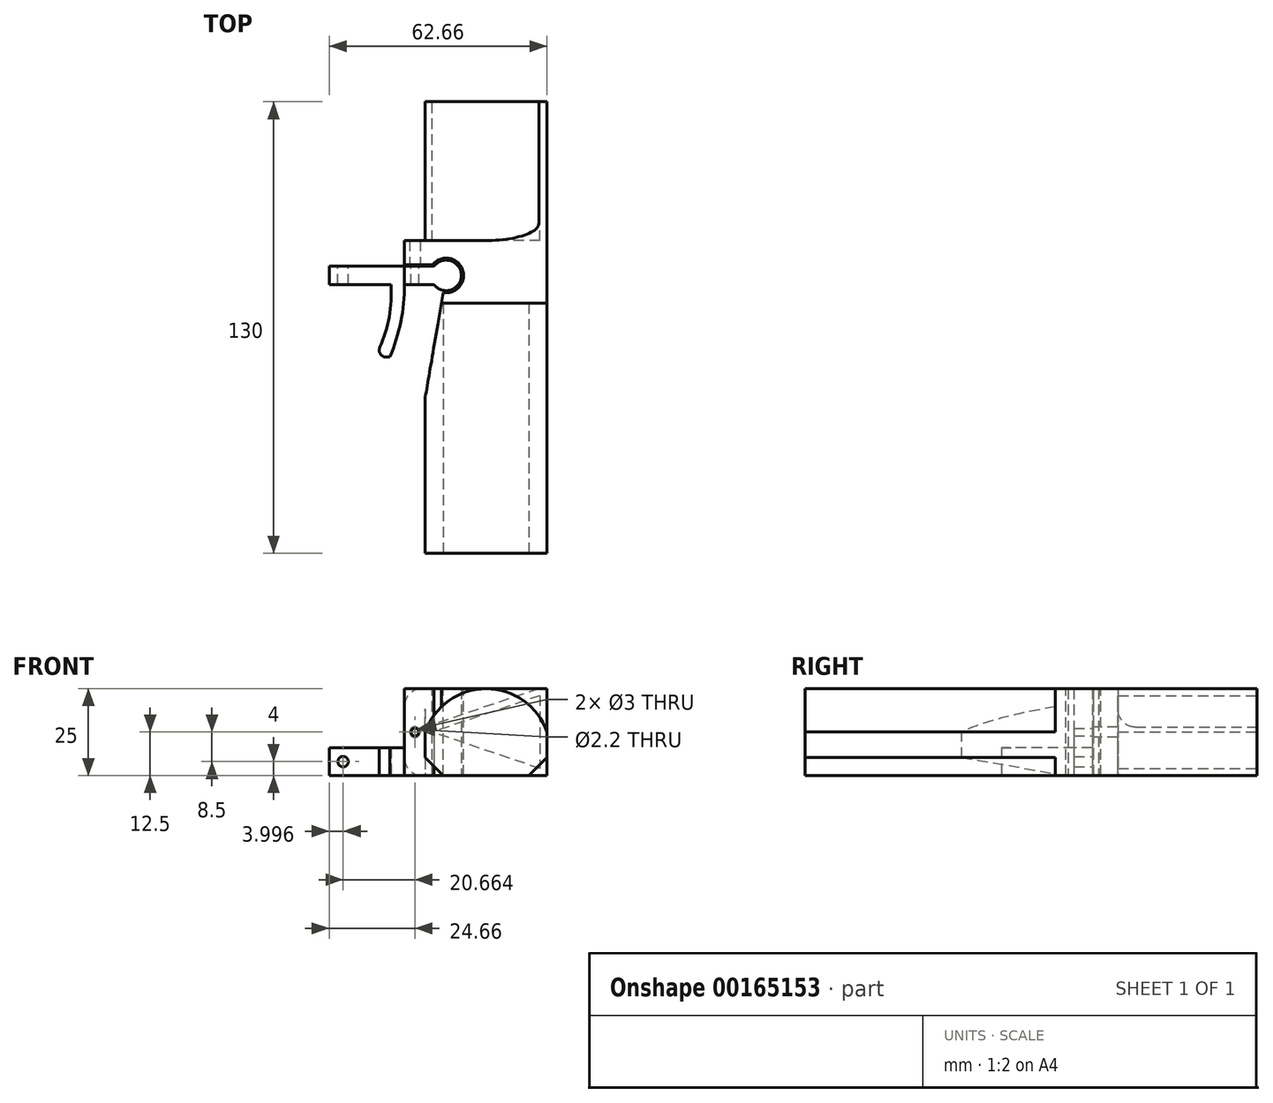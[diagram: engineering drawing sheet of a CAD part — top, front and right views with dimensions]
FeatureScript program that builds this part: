
annotation { "Feature Type Name" : "Feature", "Feature Type Description" : "" }
export const myFeature = defineFeature(function(context is Context, id is Id, definition is map)
    precondition{}
    {
        {
            var Q0;
            Q0=qCreatedBy(makeId("Top.planeOp"),FACE);
            var sketch = newSketch(context, id + "F0", { "sketchPlane" : qUnion([Q0])});
            skLineSegment(sketch, "E0.bottom", {"start": v(17.5, -50) * mm, "end": v(-17.5, -50) * mm});
            skLineSegment(sketch, "E0.top", {"start": v(17.5, 50) * mm, "end": v(-17.5, 50) * mm});
            skLineSegment(sketch, "E0.left", {"start": v(17.5, -50) * mm, "end": v(17.5, 50) * mm});
            skLineSegment(sketch, "E0.right", {"start": v(-17.5, -50) * mm, "end": v(-17.5, 50) * mm});
            skPoint(sketch, "E0.middle", {"position": v(0, 0) * mm});
            skSolve(sketch);
        }
        {
            var Q0;
            Q0 = qSketchRegion(id + "F0", true);
            extrude(context, id + "F1", {"entities" : qUnion([Q0]), "depth" : 25 * mm});
        }
        {
            var Q0;
            Q0=makeQuery(id+"F1.opExtrude","SWEPT_FACE",FACE,{"disambiguationData":[OSD([sQuery(id+"F0.wireOp",EDGE,"E0.top")])]});
            var sketch = newSketch(context, id + "F2", { "sketchPlane" : qUnion([Q0])});
            skLineSegment(sketch, "E1", {"start": v(-17.5, 12.5) * mm, "end": v(-15.5, 12.5) * mm, "construction": true});
            skLineSegment(sketch, "E2", {"start": v(17.5, 12.5) * mm, "end": v(15.5, 12.5) * mm, "construction": true});
            skLineSegment(sketch, "E3", {"start": v(-15.5, 23) * mm, "end": v(-15.5, 2) * mm});
            skLineSegment(sketch, "E4", {"start": v(-15.5, 2) * mm, "end": v(15.5, 12.5) * mm});
            skLineSegment(sketch, "E5", {"start": v(-15.5, 23) * mm, "end": v(15.5, 12.5) * mm});
            skLineSegment(sketch, "E6", {"start": v(-15.5, 23) * mm, "end": v(-15.5, 25) * mm, "construction": true});
            skLineSegment(sketch, "E7", {"start": v(-15.17, 25) * mm, "end": v(17.5, 13.93) * mm});
            skLineSegment(sketch, "E8", {"start": v(17.5, 13.93) * mm, "end": v(17.5, 25) * mm});
            skLineSegment(sketch, "E9", {"start": v(17.5, 25) * mm, "end": v(-15.17, 25) * mm});
            skLineSegment(sketch, "E10", {"start": v(0, 17.75) * mm, "end": v(0.64, 19.64) * mm, "construction": true});
            skSolve(sketch);
        }
        {
            var Q0;
            Q0 = qSketchRegion(id + "F2", true);
            extrude(context, id + "F3", {"entities" : qUnion([Q0]), "operationType" : NewBodyOperationType.REMOVE, "oppositeDirection" : true, "depth" : 40 * mm});
        }
        {
            var Q0;
            Q0=makeQuery(id+"F1.opExtrude","CAP_FACE",FACE,{"disambiguationData":[OSD([sQuery(id+"F0.wireOp",EDGE,"E0.bottom"),sQuery(id+"F0.wireOp",EDGE,"E0.top"),sQuery(id+"F0.wireOp",EDGE,"E0.left"),sQuery(id+"F0.wireOp",EDGE,"E0.right")])],"isStart":false});
            var sketch = newSketch(context, id + "F4", { "sketchPlane" : qUnion([Q0])});
            skLineSegment(sketch, "E11", {"start": v(-11.5, 10) * mm, "end": v(-11.5, 0) * mm, "construction": true});
            skLineSegment(sketch, "E12", {"start": v(-11.5, 10) * mm, "end": v(-17.5, 10) * mm, "construction": true});
            skCircle(sketch, "E13", {"center": v(-11.5, 0) * mm, "radius": 5 * mm});
            skLineSegment(sketch, "E14", {"start": v(-16.5, 0) * mm, "end": v(-17.5, 0) * mm, "construction": true});
            skLineSegment(sketch, "E15.bottom", {"start": v(-15.5, 3) * mm, "end": v(-19.5, 3) * mm});
            skLineSegment(sketch, "E15.top", {"start": v(-15.5, -3) * mm, "end": v(-19.5, -3) * mm});
            skLineSegment(sketch, "E15.left", {"start": v(-15.5, 3) * mm, "end": v(-15.5, -3) * mm});
            skLineSegment(sketch, "E15.right", {"start": v(-19.5, 3) * mm, "end": v(-19.5, -3) * mm});
            skPoint(sketch, "E15.middle", {"position": v(-17.5, 0) * mm});
            skLineSegment(sketch, "E16", {"start": v(-17.5, -3) * mm, "end": v(-17.5, -35) * mm});
            skLineSegment(sketch, "E17", {"start": v(-17.5, -50) * mm, "end": v(-17.5, -35) * mm, "construction": true});
            skLineSegment(sketch, "E18", {"start": v(-17.5, -35) * mm, "end": v(-12.34, -4.93) * mm});
            skSolve(sketch);
        }
        {
            var Q0;
            Q0 = qSketchRegion(id + "F4", true);
            extrude(context, id + "F5", {"entities" : qUnion([Q0]), "operationType" : NewBodyOperationType.REMOVE, "endBound" : BoundingType.THROUGH_ALL, "oppositeDirection" : true, "depth" : 25 * mm});
        }
        {
            var Q0;
            Q0=makeQuery(id+"F5.boolean.opBoolean","COPY",FACE,{"derivedFrom":makeQuery(id+"F5.opExtrude","SWEPT_FACE",FACE,{"disambiguationData":[OSD([sQuery(id+"F4.wireOp",EDGE,"E15.bottom")])]})});
            var sketch = newSketch(context, id + "F6", { "sketchPlane" : qUnion([Q0])});
            skLineSegment(sketch, "E19", {"start": v(-17.5, 12.5) * mm, "end": v(-20.5, 12.5) * mm, "construction": true});
            skCircle(sketch, "E20", {"center": v(-20.5, 12.5) * mm, "radius": 1.5 * mm});
            skLineSegment(sketch, "E21.bottom", {"start": v(-17.5, 0) * mm, "end": v(-23.5, 0) * mm});
            skLineSegment(sketch, "E21.top", {"start": v(-17.5, 25) * mm, "end": v(-23.5, 25) * mm});
            skLineSegment(sketch, "E21.left", {"start": v(-17.5, 0) * mm, "end": v(-17.5, 25) * mm});
            skLineSegment(sketch, "E21.right", {"start": v(-23.5, 0) * mm, "end": v(-23.5, 25) * mm});
            skSolve(sketch);
        }
        {
            var Q0;
            Q0 = qSketchRegion(id + "F6", true);
            var Q1;
            Q1=makeQuery(id+"F3.boolean.opBoolean","COPY",FACE,{"derivedFrom":makeQuery(id+"F3.opExtrude","CAP_FACE",FACE,{"disambiguationData":[OSD([sQuery(id+"F2.wireOp",EDGE,"E7"),sQuery(id+"F2.wireOp",EDGE,"E8"),sQuery(id+"F2.wireOp",EDGE,"E9")])],"isStart":false})});
            extrude(context, id + "F7", {"entities" : qUnion([Q0]), "operationType" : NewBodyOperationType.ADD, "endBound" : BoundingType.UP_TO_SURFACE, "oppositeDirection" : true, "endBoundEntityFace" : qUnion([Q1]), "depth" : 6 * mm});
        }
        {
            var Q0;
            Q0=qCreatedBy(makeId("Top.planeOp"),FACE);
            var sketch = newSketch(context, id + "F8", { "sketchPlane" : qUnion([Q0])});
            skLineSegment(sketch, "E22.0", {"start": v(-15.5, 3) * mm, "end": v(-15.5, 3) * mm});
            skArc(sketch, "E23.0", {"start": v(-15.02, -2.64) * mm, "mid": v(-7.1, 0) * mm, "end": v(-15.02, 2.64) * mm});
            skLineSegment(sketch, "E24.0", {"start": v(-15.5, 3) * mm, "end": v(-23.5, 3) * mm, "construction": true});
            skLineSegment(sketch, "E25", {"start": v(-15.02, 2.64) * mm, "end": v(-23.5, 2.64) * mm});
            skLineSegment(sketch, "E26", {"start": v(-23.5, 2.64) * mm, "end": v(-23.5, -2.64) * mm});
            skLineSegment(sketch, "E27", {"start": v(-23.5, -2.64) * mm, "end": v(-15.02, -2.64) * mm});
            skSolve(sketch);
        }
        {
            var Q0;
            Q0 = qSketchRegion(id + "F8", true);
            var Q1;
            Q1=makeQuery(id+"F7.boolean.opBoolean","MERGE",FACE,{"derivedFrom":[makeQuery(id+"F1.opExtrude","CAP_FACE",FACE,{"disambiguationData":[OSD([sQuery(id+"F0.wireOp",EDGE,"E0.bottom"),sQuery(id+"F0.wireOp",EDGE,"E0.top"),sQuery(id+"F0.wireOp",EDGE,"E0.left"),sQuery(id+"F0.wireOp",EDGE,"E0.right")])],"isStart":false}),makeQuery(id+"F7.opExtrude","SWEPT_FACE",FACE,{"disambiguationData":[OSD([sQuery(id+"F6.wireOp",EDGE,"E21.top")])]})]});
            extrude(context, id + "F9", {"entities" : qUnion([Q0]), "endBound" : BoundingType.UP_TO_SURFACE, "endBoundEntityFace" : qUnion([Q1]), "depth" : 25 * mm});
        }
        {
            var Q0;
            Q0=makeQuery(id+"F9.opExtrude","SWEPT_FACE",FACE,{"disambiguationData":[OSD([sQuery(id+"F8.wireOp",EDGE,"E25")])]});
            var sketch = newSketch(context, id + "F10", { "sketchPlane" : qUnion([Q0])});
            skCircle(sketch, "E28.0", {"center": v(20.5, 12.5) * mm, "radius": 1.5 * mm, "construction": true});
            skCircle(sketch, "E29.0", {"center": v(20.5, 12.5) * mm, "radius": 1.1 * mm});
            skSolve(sketch);
        }
        {
            var Q0;
            Q0 = qSketchRegion(id + "F10", true);
            extrude(context, id + "F11", {"entities" : qUnion([Q0]), "operationType" : NewBodyOperationType.REMOVE, "endBound" : BoundingType.THROUGH_ALL, "oppositeDirection" : true, "depth" : 25 * mm});
        }
        {
            var Q0;
            Q0=makeQuery(id+"F9.opExtrude","CAP_FACE",FACE,{"disambiguationData":[OSD([sQuery(id+"F8.wireOp",EDGE,"E23.0"),sQuery(id+"F8.wireOp",EDGE,"E25"),sQuery(id+"F8.wireOp",EDGE,"E26"),sQuery(id+"F8.wireOp",EDGE,"E27")])],"isStart":true});
            var sketch = newSketch(context, id + "F12", { "sketchPlane" : qUnion([Q0])});
            skLineSegment(sketch, "E30", {"start": v(-27.7, 23.54) * mm, "end": v(-31.96, 23.54) * mm});
            skLineSegment(sketch, "E31", {"start": v(-23.5, -2.64) * mm, "end": v(-23.5, 2.64) * mm});
            skArc(sketch, "E32", {"start": v(-27.35, 2.64) * mm, "mid": v(-28.19, 13.42) * mm, "end": v(-31.96, 23.54) * mm});
            skArc(sketch, "E33", {"start": v(-23.5, 2.64) * mm, "mid": v(-24.56, 13.3) * mm, "end": v(-27.7, 23.54) * mm});
            skLineSegment(sketch, "E34", {"start": v(-23.5, -2.64) * mm, "end": v(-45.16, -2.64) * mm});
            skLineSegment(sketch, "E35", {"start": v(-45.16, -2.64) * mm, "end": v(-45.16, 2.64) * mm});
            skLineSegment(sketch, "E36", {"start": v(-45.16, 2.64) * mm, "end": v(-27.35, 2.64) * mm});
            skSolve(sketch);
        }
        {
            var Q0;
            Q0 = qSketchRegion(id + "F12", true);
            extrude(context, id + "F13", {"entities" : qUnion([Q0]), "operationType" : NewBodyOperationType.ADD, "oppositeDirection" : true, "depth" : 8 * mm});
        }
        {
            var Q0;
            Q0=makeQuery(id+"F13.opExtrude","SWEPT_EDGE",EDGE,{"disambiguationData":[OSD([sQuery(id+"F12.wireOp",EDGE,"E30"),sQuery(id+"F12.wireOp",EDGE,"E32")])]});
            var Q1;
            Q1=makeQuery(id+"F13.opExtrude","CAP_EDGE",EDGE,{"disambiguationData":[OSD([sQuery(id+"F12.wireOp",EDGE,"E31")])],"isStart":false});
            var Q2;
            Q2=makeQuery(id+"F9.opExtrude","TWEAK_EDGE",EDGE,{"derivedFrom":[makeQuery(id+"F7.boolean.opBoolean","MERGE",FACE,{"derivedFrom":[makeQuery(id+"F1.opExtrude","CAP_FACE",FACE,{"disambiguationData":[OSD([sQuery(id+"F0.wireOp",EDGE,"E0.bottom"),sQuery(id+"F0.wireOp",EDGE,"E0.top"),sQuery(id+"F0.wireOp",EDGE,"E0.left"),sQuery(id+"F0.wireOp",EDGE,"E0.right")])],"isStart":false}),makeQuery(id+"F7.opExtrude","SWEPT_FACE",FACE,{"disambiguationData":[OSD([sQuery(id+"F6.wireOp",EDGE,"E21.top")])]})]}),makeQuery(id+"F8.imprint","IMPRINT",EDGE,{"derivedFrom":sQuery(id+"F8.wireOp",EDGE,"E26")})]});
            fillet(context, id + "F14", {"entities" : qUnion([Q0, Q1, Q2]), "radius" : 2 * mm, "tangentPropagation" : true, "allowEdgeOverflow" : false});
        }
        {
            var Q0;
            Q0=makeQuery(id+"F1.opExtrude","SWEPT_FACE",FACE,{"disambiguationData":[OSD([sQuery(id+"F0.wireOp",EDGE,"E0.bottom")])]});
            extrude(context, id + "F15", {"entities" : qUnion([Q0]), "operationType" : NewBodyOperationType.ADD, "depth" : 30 * mm});
        }
        {
            var Q0;
            Q0=makeQuery(id+"F15.opExtrude","CAP_FACE",FACE,{"disambiguationData":[OSD([sQuery(id+"F0.wireOp",EDGE,"E0.bottom")])],"isStart":false});
            var sketch = newSketch(context, id + "F16", { "sketchPlane" : qUnion([Q0])});
            skArc(sketch, "E37", {"start": v(17.5, 12.5) * mm, "mid": v(0, 25) * mm, "end": v(-17.5, 12.5) * mm});
            skLineSegment(sketch, "E38", {"start": v(-17.5, 5.18) * mm, "end": v(-12.32, 0) * mm});
            skLineSegment(sketch, "E39", {"start": v(-12.32, 0) * mm, "end": v(12.32, 0) * mm});
            skLineSegment(sketch, "E40", {"start": v(12.32, 0) * mm, "end": v(17.5, 5.18) * mm});
            skLineSegment(sketch, "E41", {"start": v(17.5, 5.18) * mm, "end": v(17.5, 12.5) * mm});
            skLineSegment(sketch, "E42", {"start": v(-17.5, 12.5) * mm, "end": v(-17.5, 5.18) * mm});
            skLineSegment(sketch, "E43", {"start": v(-17.5, 5.18) * mm, "end": v(-17.5, 0) * mm});
            skLineSegment(sketch, "E44", {"start": v(-17.5, 0) * mm, "end": v(-12.32, 0) * mm});
            skLineSegment(sketch, "E45", {"start": v(12.32, 0) * mm, "end": v(17.5, 0) * mm});
            skLineSegment(sketch, "E46", {"start": v(17.5, 0) * mm, "end": v(17.5, 5.18) * mm});
            skLineSegment(sketch, "E47", {"start": v(17.5, 12.5) * mm, "end": v(17.5, 25) * mm});
            skLineSegment(sketch, "E48", {"start": v(17.5, 25) * mm, "end": v(0, 25) * mm});
            skLineSegment(sketch, "E49", {"start": v(0, 25) * mm, "end": v(-17.5, 25) * mm});
            skLineSegment(sketch, "E50", {"start": v(-17.5, 25) * mm, "end": v(-17.5, 12.5) * mm});
            skSolve(sketch);
        }
        {
            var Q0;
            {var subQ0=sQuery(id+"F16.wireOp",EDGE,"E47");Q0=makeQuery(id+"F16.imprint","IMPRINT",FACE,{"disambiguationData":[TD([[makeQuery(id+"F16.imprint","IMPRINT",EDGE,{"derivedFrom":subQ0}),-1.0]])]});}
            var Q1;
            {var subQ2=sQuery(id+"F16.wireOp",EDGE,"E49");Q1=makeQuery(id+"F16.imprint","IMPRINT",FACE,{"disambiguationData":[TD([[makeQuery(id+"F16.imprint","IMPRINT",EDGE,{"derivedFrom":subQ2}),1.0]])]});}
            var Q2;
            Q2=makeQuery(id+"F16.imprint","IMPRINT",FACE,{"disambiguationData":[TD([[makeQuery(id+"F16.imprint","IMPRINT",EDGE,{"derivedFrom":sQuery(id+"F16.wireOp",EDGE,"E38")}),-1.0]])]});
            var Q3;
            Q3=makeQuery(id+"F16.imprint","IMPRINT",FACE,{"disambiguationData":[TD([[makeQuery(id+"F16.imprint","IMPRINT",EDGE,{"derivedFrom":sQuery(id+"F16.wireOp",EDGE,"E40")}),-1.0]])]});
            extrude(context, id + "F17", {"entities" : qUnion([Q0, Q1, Q2, Q3]), "operationType" : NewBodyOperationType.REMOVE, "oppositeDirection" : true, "depth" : 72 * mm});
        }
        {
            var Q0;
            Q0=makeQuery(id+"F17.boolean.opBoolean","COPY",EDGE,{"derivedFrom":makeQuery(id+"F17.opExtrude","CAP_EDGE",EDGE,{"disambiguationData":[OSD([sQuery(id+"F16.wireOp",EDGE,"E47")])],"isStart":false})});
            var Q1;
            Q1=makeQuery(id+"F17.boolean.opBoolean","COPY",EDGE,{"derivedFrom":makeQuery(id+"F17.opExtrude","CAP_EDGE",EDGE,{"disambiguationData":[OSD([sQuery(id+"F16.wireOp",EDGE,"E46")])],"isStart":false})});
            var Q2;
            Q2=makeQuery(id+"F3.boolean.opBoolean","COPY",EDGE,{"derivedFrom":makeQuery(id+"F3.opExtrude","CAP_EDGE",EDGE,{"disambiguationData":[OSD([sQuery(id+"F2.wireOp",EDGE,"E7")])],"isStart":false})});
            var Q3;
            Q3=makeQuery(id+"F7.opExtrude","SWEPT_EDGE",EDGE,{"disambiguationData":[OSD([sQuery(id+"F6.wireOp",EDGE,"E21.bottom"),sQuery(id+"F6.wireOp",EDGE,"E21.right")])]});
            var Q4;
            Q4=makeQuery(id+"F7.opExtrude","SWEPT_EDGE",EDGE,{"disambiguationData":[OSD([sQuery(id+"F6.wireOp",EDGE,"E21.top"),sQuery(id+"F6.wireOp",EDGE,"E21.right")])]});
            fillet(context, id + "F18", {"entities" : qUnion([Q0, Q1, Q2, Q3, Q4]), "radius" : 5 * mm, "tangentPropagation" : true, "allowEdgeOverflow" : false});
        }
        {
            var Q0;
            Q0=makeQuery(id+"F13.boolean.opBoolean","MERGE",FACE,{"derivedFrom":[makeQuery(id+"F9.opExtrude","SWEPT_FACE",FACE,{"disambiguationData":[OSD([sQuery(id+"F8.wireOp",EDGE,"E25")])]}),makeQuery(id+"F13.opExtrude","SWEPT_FACE",FACE,{"disambiguationData":[OSD([sQuery(id+"F12.wireOp",EDGE,"E34")])]})]});
            var sketch = newSketch(context, id + "F19", { "sketchPlane" : qUnion([Q0])});
            skLineSegment(sketch, "E51", {"start": v(45.16, 4) * mm, "end": v(41.16, 4) * mm, "construction": true});
            skLineSegment(sketch, "E52", {"start": v(41.16, 4) * mm, "end": v(41.16, 8) * mm, "construction": true});
            skCircle(sketch, "E53", {"center": v(41.16, 4) * mm, "radius": 1.5 * mm});
            skCircle(sketch, "E54.0", {"center": v(20.5, 12.5) * mm, "radius": 1.5 * mm, "construction": true});
            skSolve(sketch);
        }
        {
            var Q0;
            Q0 = qSketchRegion(id + "F19", true);
            extrude(context, id + "F20", {"entities" : qUnion([Q0]), "operationType" : NewBodyOperationType.REMOVE, "endBound" : BoundingType.THROUGH_ALL, "oppositeDirection" : true, "depth" : 25 * mm});
        }
    });
